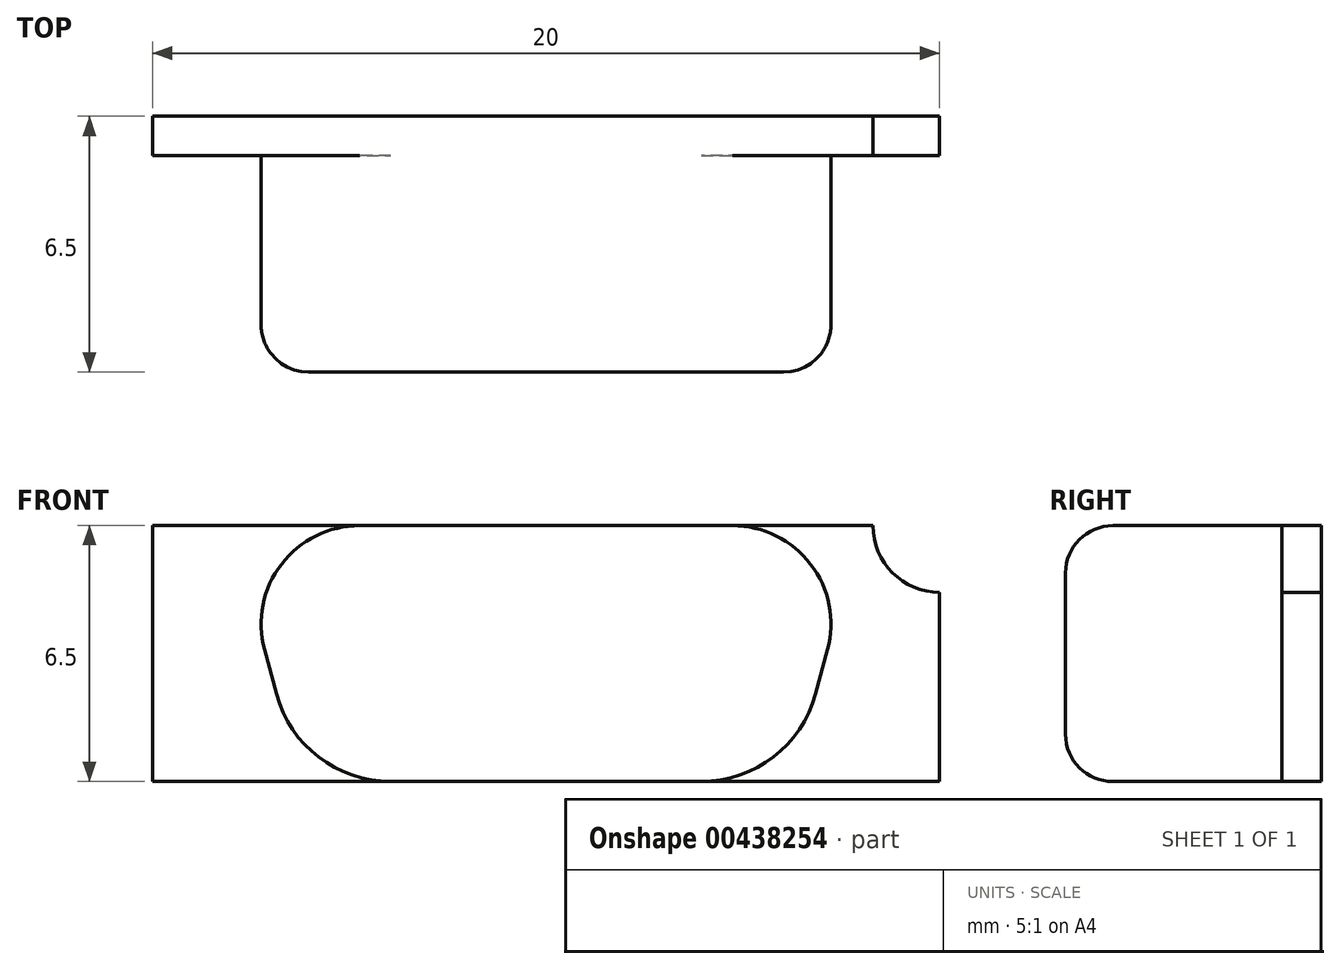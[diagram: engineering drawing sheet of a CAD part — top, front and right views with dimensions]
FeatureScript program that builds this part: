
annotation { "Feature Type Name" : "Feature", "Feature Type Description" : "" }
export const myFeature = defineFeature(function(context is Context, id is Id, definition is map)
    precondition{}
    {
        {
            var Q0;
            Q0=qCreatedBy(makeId("Front.planeOp"),FACE);
            var sketch = newSketch(context, id + "F0", { "sketchPlane" : qUnion([Q0])});
            skLineSegment(sketch, "E0", {"start": v(-10.96, 0.03) * mm, "end": v(9.04, 0.03) * mm});
            skLineSegment(sketch, "E1", {"start": v(9.04, 0.03) * mm, "end": v(9.04, -7.97) * mm});
            skLineSegment(sketch, "E2", {"start": v(9.04, -7.97) * mm, "end": v(-10.96, -7.97) * mm});
            skLineSegment(sketch, "E3", {"start": v(-10.96, -7.97) * mm, "end": v(-10.96, 0.03) * mm});
            skSolve(sketch);
        }
        {
            var Q0;
            Q0=makeQuery(id+"F0.imprint","IMPRINT",FACE,{"disambiguationData":[TD([[makeQuery(id+"F0.imprint","IMPRINT",EDGE,{"derivedFrom":sQuery(id+"F0.wireOp",EDGE,"E0")}),-1.0]])]});
            extrude(context, id + "F1", {"entities" : qUnion([Q0]), "depth" : 1 * mm});
        }
        {
            var Q0;
            Q0=makeQuery(id+"F1.opExtrude","CAP_FACE",FACE,{"disambiguationData":[OSD([sQuery(id+"F0.wireOp",EDGE,"E0"),sQuery(id+"F0.wireOp",EDGE,"E1"),sQuery(id+"F0.wireOp",EDGE,"E2"),sQuery(id+"F0.wireOp",EDGE,"E3")])],"isStart":false});
            var sketch = newSketch(context, id + "F2", { "sketchPlane" : qUnion([Q0])});
            skLineSegment(sketch, "E4", {"start": v(-8.96, 0.03) * mm, "end": v(7.04, 0.03) * mm});
            skLineSegment(sketch, "E5", {"start": v(7.04, 0.03) * mm, "end": v(5.3, -6.47) * mm});
            skLineSegment(sketch, "E6", {"start": v(5.3, -6.47) * mm, "end": v(-7.2, -6.47) * mm});
            skLineSegment(sketch, "E7", {"start": v(-7.2, -6.47) * mm, "end": v(-8.96, 0.03) * mm});
            skSolve(sketch);
        }
        {
            var Q0;
            Q0 = qSketchRegion(id + "F2", true);
            extrude(context, id + "F3", {"entities" : qUnion([Q0]), "operationType" : NewBodyOperationType.ADD, "depth" : 5.5 * mm});
        }
        {
            var Q0;
            Q0=makeQuery(id+"F3.opExtrude","SWEPT_EDGE",EDGE,{"disambiguationData":[OSD([sQuery(id+"F0.wireOp",EDGE,"E0"),sQuery(id+"F2.wireOp",EDGE,"E4"),sQuery(id+"F2.wireOp",EDGE,"E5")])]});
            var Q1;
            Q1=makeQuery(id+"F3.opExtrude","SWEPT_EDGE",EDGE,{"disambiguationData":[OSD([sQuery(id+"F0.wireOp",EDGE,"E0"),sQuery(id+"F2.wireOp",EDGE,"E4"),sQuery(id+"F2.wireOp",EDGE,"E7")])]});
            fillet(context, id + "F4", {"entities" : qUnion([Q0, Q1]), "radius" : 2.5 * mm, "tangentPropagation" : true, "allowEdgeOverflow" : false});
        }
        {
            var Q0;
            Q0=makeQuery(id+"F3.opExtrude","SWEPT_EDGE",EDGE,{"disambiguationData":[OSD([sQuery(id+"F0.wireOp",EDGE,"E2"),sQuery(id+"F2.wireOp",EDGE,"E5"),sQuery(id+"F2.wireOp",EDGE,"E6")])]});
            var Q1;
            Q1=makeQuery(id+"F3.opExtrude","SWEPT_EDGE",EDGE,{"disambiguationData":[OSD([sQuery(id+"F0.wireOp",EDGE,"E2"),sQuery(id+"F2.wireOp",EDGE,"E6"),sQuery(id+"F2.wireOp",EDGE,"E7")])]});
            fillet(context, id + "F5", {"entities" : qUnion([Q0, Q1]), "radius" : 3 * mm, "tangentPropagation" : true, "allowEdgeOverflow" : false});
        }
        {
            var Q0;
            Q0=makeQuery(id+"F3.opExtrude","CAP_FACE",FACE,{"disambiguationData":[OSD([sQuery(id+"F2.wireOp",EDGE,"E4"),sQuery(id+"F2.wireOp",EDGE,"E5"),sQuery(id+"F2.wireOp",EDGE,"E6"),sQuery(id+"F2.wireOp",EDGE,"E7")])],"isStart":false});
            fillet(context, id + "F6", {"entities" : qUnion([Q0]), "radius" : 1.2 * mm, "tangentPropagation" : true, "allowEdgeOverflow" : false});
        }
        {
            var Q0;
            Q0=makeQuery(id+"F1.opExtrude","CAP_FACE",FACE,{"disambiguationData":[OSD([sQuery(id+"F0.wireOp",EDGE,"E0"),sQuery(id+"F0.wireOp",EDGE,"E1"),sQuery(id+"F0.wireOp",EDGE,"E2"),sQuery(id+"F0.wireOp",EDGE,"E3")])],"isStart":false});
            var sketch = newSketch(context, id + "F7", { "sketchPlane" : qUnion([Q0])});
            skPoint(sketch, "E8.oppositeSnap0", {"position": v(-0.96, -6.47) * mm});
            skLineSegment(sketch, "E8.bottom", {"start": v(9.04, -7.97) * mm, "end": v(-10.96, -7.97) * mm});
            skLineSegment(sketch, "E8.top", {"start": v(9.04, -6.47) * mm, "end": v(-10.96, -6.47) * mm});
            skLineSegment(sketch, "E8.left", {"start": v(9.04, -7.97) * mm, "end": v(9.04, -6.47) * mm});
            skLineSegment(sketch, "E8.right", {"start": v(-10.96, -7.97) * mm, "end": v(-10.96, -6.47) * mm});
            skSolve(sketch);
        }
        {
            var Q0;
            Q0 = qSketchRegion(id + "F7", true);
            extrude(context, id + "F8", {"entities" : qUnion([Q0]), "operationType" : NewBodyOperationType.REMOVE, "oppositeDirection" : true, "depth" : 25 * mm});
        }
        {
            var Q0;
            {var subQ2=sQuery(id+"F0.wireOp",EDGE,"E1");var subQ3=sQuery(id+"F0.wireOp",EDGE,"E0");Q0=makeQuery(id+"F8.boolean.opBoolean","SPLIT",FACE,{"disambiguationData":[TD([makeQuery(id+"F1.opExtrude","SWEPT_FACE",FACE,{"disambiguationData":[OSD([subQ2])]})])],"derivedFrom":makeQuery(id+"F1.opExtrude","CAP_FACE",FACE,{"disambiguationData":[OSD([subQ3,subQ2,sQuery(id+"F0.wireOp",EDGE,"E2"),sQuery(id+"F0.wireOp",EDGE,"E3")])],"isStart":false})});}
            var sketch = newSketch(context, id + "F9", { "sketchPlane" : qUnion([Q0])});
            skCircle(sketch, "E9", {"center": v(9.04, 0.03) * mm, "radius": 1.7 * mm});
            skSolve(sketch);
        }
        {
            var Q0;
            Q0 = qSketchRegion(id + "F9", true);
            extrude(context, id + "F10", {"entities" : qUnion([Q0]), "operationType" : NewBodyOperationType.REMOVE, "oppositeDirection" : true, "depth" : 25 * mm});
        }
    });
